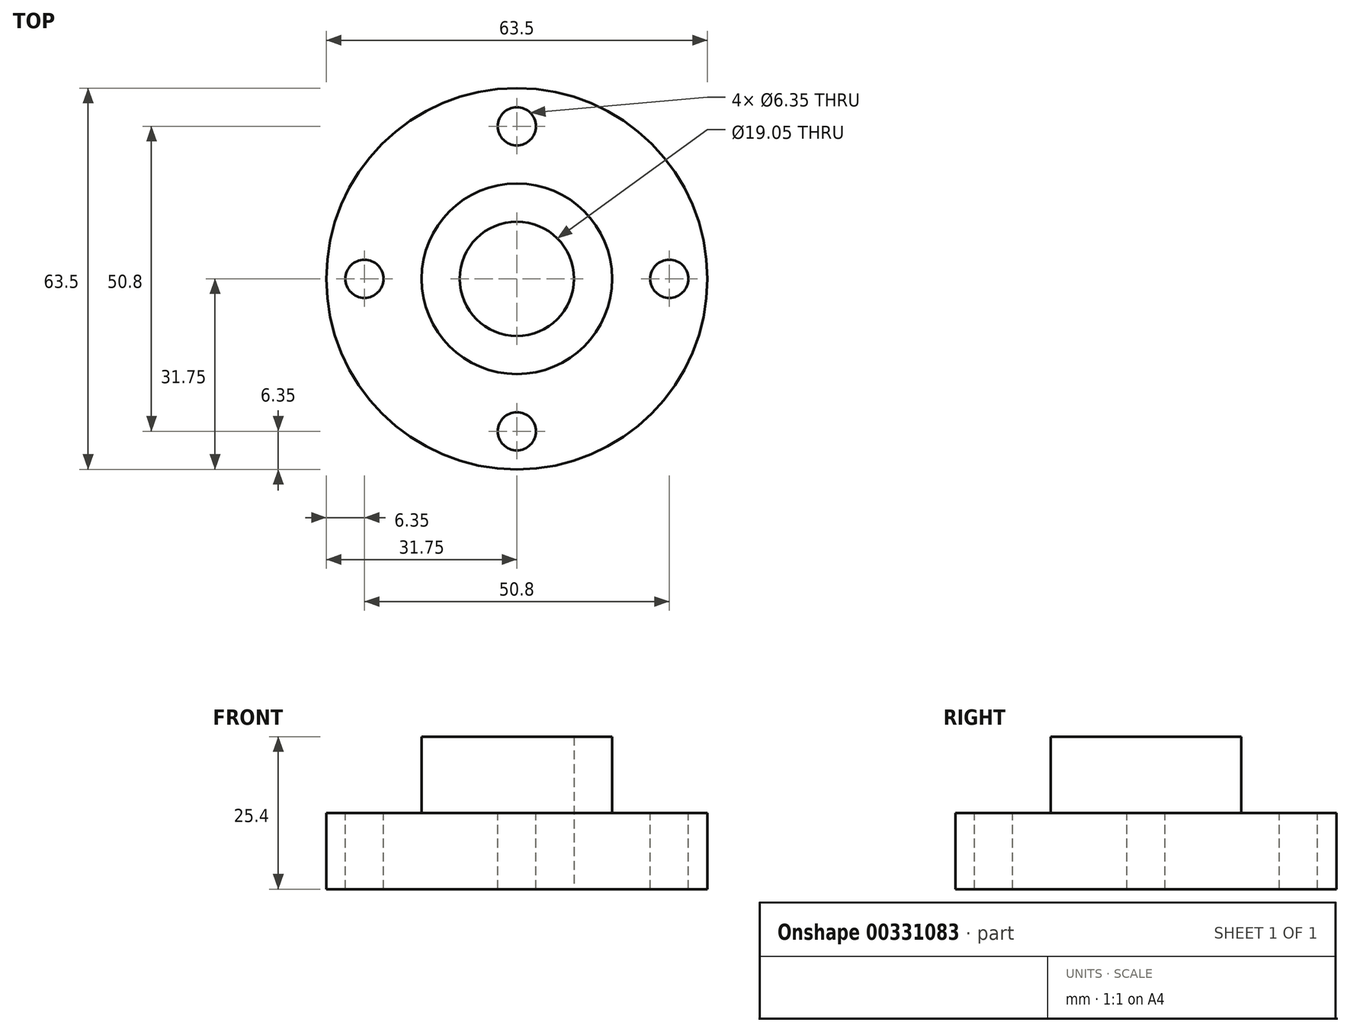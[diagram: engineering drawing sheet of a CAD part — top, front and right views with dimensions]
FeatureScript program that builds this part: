
annotation { "Feature Type Name" : "Feature", "Feature Type Description" : "" }
export const myFeature = defineFeature(function(context is Context, id is Id, definition is map)
    precondition{}
    {
        {
            var Q0;
            Q0=qCreatedBy(makeId("Top.planeOp"),FACE);
            var sketch = newSketch(context, id + "F0", { "sketchPlane" : qUnion([Q0])});
            skCircle(sketch, "E0", {"center": v(0, 0) * mm, "radius": 31.75 * mm});
            skCircle(sketch, "E1", {"center": v(0, 0) * mm, "radius": 15.88 * mm});
            skCircle(sketch, "E2", {"center": v(0, 0) * mm, "radius": 9.53 * mm});
            skSolve(sketch);
        }
        {
            var Q0;
            Q0=makeQuery(id+"F0.imprint","IMPRINT",FACE,{"disambiguationData":[TD([[makeQuery(id+"F0.imprint","IMPRINT",EDGE,{"derivedFrom":sQuery(id+"F0.wireOp",EDGE,"E0")}),1.0]])]});
            extrude(context, id + "F1", {"entities" : qUnion([Q0]), "depth" : 12.7 * mm});
        }
        {
            var Q0;
            Q0=makeQuery(id+"F0.imprint","IMPRINT",FACE,{"disambiguationData":[TD([[makeQuery(id+"F0.imprint","IMPRINT",EDGE,{"derivedFrom":sQuery(id+"F0.wireOp",EDGE,"E1")}),1.0]])]});
            extrude(context, id + "F2", {"entities" : qUnion([Q0]), "operationType" : NewBodyOperationType.ADD, "depth" : 25.4 * mm});
        }
        {
            var Q0;
            Q0=makeQuery(id+"F1.opExtrude","CAP_FACE",FACE,{"disambiguationData":[OSD([sQuery(id+"F0.wireOp",EDGE,"E0"),sQuery(id+"F0.wireOp",EDGE,"E1")])],"isStart":false});
            var sketch = newSketch(context, id + "F3", { "sketchPlane" : qUnion([Q0])});
            skCircle(sketch, "E3", {"center": v(0, 0) * mm, "radius": 25.4 * mm, "construction": true});
            skCircle(sketch, "E4", {"center": v(0, 25.4) * mm, "radius": 3.18 * mm});
            skCircle(sketch, "E5", {"center": v(-25.4, 0) * mm, "radius": 3.18 * mm});
            skCircle(sketch, "E6", {"center": v(25.4, 0) * mm, "radius": 3.18 * mm});
            skCircle(sketch, "E7", {"center": v(0, -25.4) * mm, "radius": 3.18 * mm});
            skSolve(sketch);
        }
        {
            var Q0;
            Q0 = qSketchRegion(id + "F3", true);
            extrude(context, id + "F4", {"entities" : qUnion([Q0]), "operationType" : NewBodyOperationType.REMOVE, "endBound" : BoundingType.THROUGH_ALL, "oppositeDirection" : true, "depth" : 25.4 * mm});
        }
    });
